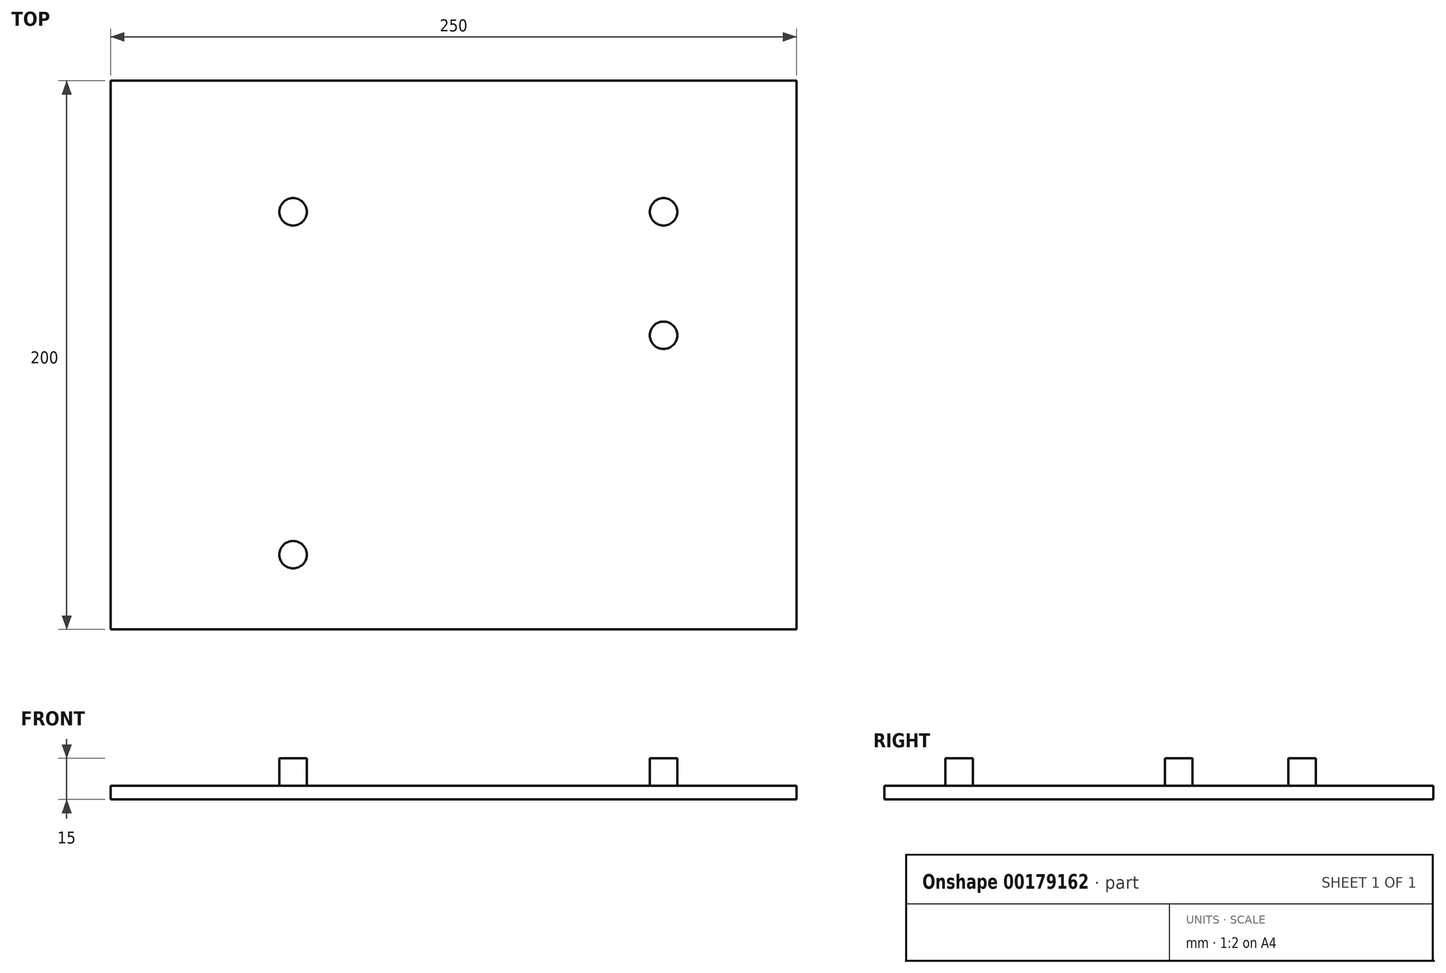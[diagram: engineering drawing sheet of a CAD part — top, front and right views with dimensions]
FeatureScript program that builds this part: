
annotation { "Feature Type Name" : "Feature", "Feature Type Description" : "" }
export const myFeature = defineFeature(function(context is Context, id is Id, definition is map)
    precondition{}
    {
        {
            var Q0;
            Q0=qCreatedBy(makeId("Top.planeOp"),FACE);
            var sketch = newSketch(context, id + "F0", { "sketchPlane" : qUnion([Q0])});
            skLineSegment(sketch, "E0.bottom", {"start": v(-72.86, 156.03) * mm, "end": v(177.14, 156.03) * mm});
            skLineSegment(sketch, "E0.top", {"start": v(-72.86, -43.97) * mm, "end": v(177.14, -43.97) * mm});
            skLineSegment(sketch, "E0.left", {"start": v(-72.86, 156.03) * mm, "end": v(-72.86, -43.97) * mm});
            skLineSegment(sketch, "E0.right", {"start": v(177.14, 156.03) * mm, "end": v(177.14, -43.97) * mm});
            skSolve(sketch);
        }
        {
            var Q0;
            Q0 = qSketchRegion(id + "F0", true);
            extrude(context, id + "F1", {"entities" : qUnion([Q0]), "depth" : 5 * mm});
        }
        {
            var Q0;
            Q0=makeQuery(id+"F1.opExtrude","CAP_FACE",FACE,{"disambiguationData":[OSD([sQuery(id+"F0.wireOp",EDGE,"E0.bottom"),sQuery(id+"F0.wireOp",EDGE,"E0.top"),sQuery(id+"F0.wireOp",EDGE,"E0.left"),sQuery(id+"F0.wireOp",EDGE,"E0.right")])],"isStart":false});
            var sketch = newSketch(context, id + "F2", { "sketchPlane" : qUnion([Q0])});
            skCircle(sketch, "E1", {"center": v(-6.35, 108.25) * mm, "radius": 5 * mm});
            skCircle(sketch, "E2", {"center": v(128.65, 108.25) * mm, "radius": 5 * mm});
            skCircle(sketch, "E3", {"center": v(-6.35, -16.75) * mm, "radius": 5 * mm});
            skCircle(sketch, "E4", {"center": v(128.65, 63.25) * mm, "radius": 5 * mm});
            skSolve(sketch);
        }
        {
            var Q0;
            Q0 = qSketchRegion(id + "F2", true);
            extrude(context, id + "F3", {"entities" : qUnion([Q0]), "operationType" : NewBodyOperationType.ADD, "depth" : 10 * mm});
        }
    });
